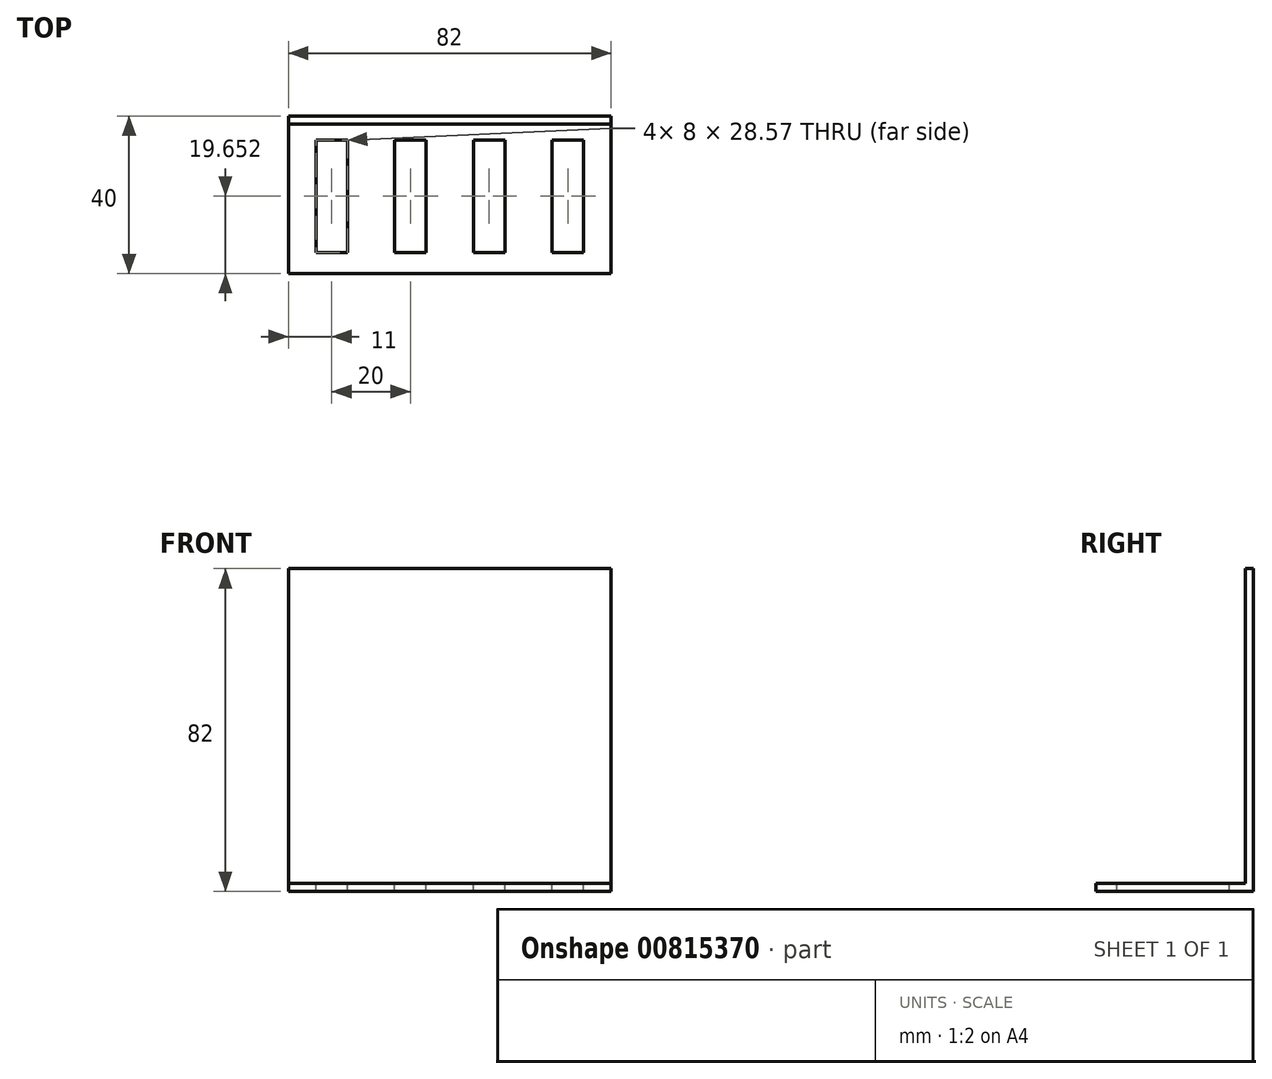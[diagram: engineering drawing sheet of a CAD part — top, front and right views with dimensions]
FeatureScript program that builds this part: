
annotation { "Feature Type Name" : "Feature", "Feature Type Description" : "" }
export const myFeature = defineFeature(function(context is Context, id is Id, definition is map)
    precondition{}
    {
        {
            var Q0;
            Q0=qCreatedBy(makeId("Right.planeOp"),FACE);
            var sketch = newSketch(context, id + "F0", { "sketchPlane" : qUnion([Q0])});
            skLineSegment(sketch, "E0", {"start": v(-48.5, 0) * mm, "end": v(-8.5, 0) * mm});
            skLineSegment(sketch, "E1", {"start": v(-8.5, 0) * mm, "end": v(-8.5, 82) * mm});
            skSolve(sketch);
        }
        {
            var Q0;
            Q0=sQuery(id+"F0.wireOp",EDGE,"E1");
            var Q1;
            Q1=sQuery(id+"F0.wireOp",EDGE,"E0");
            extrude(context, id + "F1", {"bodyType" : ToolBodyType.SURFACE, "surfaceEntities" : qUnion([Q0, Q1]), "depth" : 82 * mm, "offsetDistance" : 25 * mm});
        }
        {
            var Q0;
            Q0=makeQuery(id+"F1.opExtrude","SWEPT_FACE",FACE,{"disambiguationData":[OSD([sQuery(id+"F0.wireOp",EDGE,"E0")])]});
            extrude(context, id + "F2", {"entities" : qUnion([Q0]), "depth" : -2 * mm, "offsetDistance" : 25 * mm});
        }
        {
            var Q0;
            Q0=makeQuery(id+"F1.opExtrude","SWEPT_FACE",FACE,{"disambiguationData":[OSD([sQuery(id+"F0.wireOp",EDGE,"E1")])]});
            extrude(context, id + "F3", {"entities" : qUnion([Q0]), "operationType" : NewBodyOperationType.ADD, "depth" : -2 * mm, "offsetDistance" : 25 * mm});
        }
        {
            var Q0;
            Q0=makeQuery(id+"F2.opExtrude","CAP_FACE",FACE,{"disambiguationData":[OSD([sQuery(id+"F0.wireOp",EDGE,"E0")])],"isStart":false});
            var sketch = newSketch(context, id + "F4", { "sketchPlane" : qUnion([Q0])});
            skLineSegment(sketch, "E2.bottom", {"start": v(7, -14.57) * mm, "end": v(15, -14.57) * mm});
            skLineSegment(sketch, "E2.top", {"start": v(7, -43.14) * mm, "end": v(15, -43.14) * mm});
            skLineSegment(sketch, "E2.left", {"start": v(7, -14.57) * mm, "end": v(7, -43.14) * mm});
            skLineSegment(sketch, "E2.right", {"start": v(15, -14.57) * mm, "end": v(15, -43.14) * mm});
            skLineSegment(sketch, "E3.bottom", {"start": v(75, -14.57) * mm, "end": v(67, -14.57) * mm});
            skLineSegment(sketch, "E3.top", {"start": v(75, -43.14) * mm, "end": v(67, -43.14) * mm});
            skLineSegment(sketch, "E3.left", {"start": v(75, -14.57) * mm, "end": v(75, -43.14) * mm});
            skLineSegment(sketch, "E3.right", {"start": v(67, -14.57) * mm, "end": v(67, -43.14) * mm});
            skLineSegment(sketch, "E4.bottom", {"start": v(47, -14.57) * mm, "end": v(55, -14.57) * mm});
            skLineSegment(sketch, "E4.top", {"start": v(47, -43.14) * mm, "end": v(55, -43.14) * mm});
            skLineSegment(sketch, "E4.left", {"start": v(47, -14.57) * mm, "end": v(47, -43.14) * mm});
            skLineSegment(sketch, "E4.right", {"start": v(55, -14.57) * mm, "end": v(55, -43.14) * mm});
            skLineSegment(sketch, "E5.bottom", {"start": v(27, -14.57) * mm, "end": v(35, -14.57) * mm});
            skLineSegment(sketch, "E5.top", {"start": v(27, -43.14) * mm, "end": v(35, -43.14) * mm});
            skLineSegment(sketch, "E5.left", {"start": v(27, -14.57) * mm, "end": v(27, -43.14) * mm});
            skLineSegment(sketch, "E5.right", {"start": v(35, -14.57) * mm, "end": v(35, -43.14) * mm});
            skSolve(sketch);
        }
        {
            var Q0;
            Q0=makeQuery(id+"F4.imprint","IMPRINT",FACE,{"disambiguationData":[TD([[makeQuery(id+"F4.imprint","IMPRINT",EDGE,{"derivedFrom":sQuery(id+"F4.wireOp",EDGE,"E3.bottom")}),1.0]])]});
            var Q1;
            Q1=makeQuery(id+"F4.imprint","IMPRINT",FACE,{"disambiguationData":[TD([[makeQuery(id+"F4.imprint","IMPRINT",EDGE,{"derivedFrom":sQuery(id+"F4.wireOp",EDGE,"E4.bottom")}),-1.0]])]});
            var Q2;
            Q2=makeQuery(id+"F4.imprint","IMPRINT",FACE,{"disambiguationData":[TD([[makeQuery(id+"F4.imprint","IMPRINT",EDGE,{"derivedFrom":sQuery(id+"F4.wireOp",EDGE,"E5.bottom")}),-1.0]])]});
            var Q3;
            Q3=makeQuery(id+"F4.imprint","IMPRINT",FACE,{"disambiguationData":[TD([[makeQuery(id+"F4.imprint","IMPRINT",EDGE,{"derivedFrom":sQuery(id+"F4.wireOp",EDGE,"E2.bottom")}),-1.0]])]});
            extrude(context, id + "F5", {"entities" : qUnion([Q0, Q1, Q2, Q3]), "operationType" : NewBodyOperationType.REMOVE, "endBound" : BoundingType.THROUGH_ALL, "oppositeDirection" : true, "depth" : 2 * mm, "offsetDistance" : 25 * mm});
        }
    });
